# Revit family: Building-IEC309Connections-GEWISS-67IB-INTERLOCKED-SOCKET-OUTLETS_IP67_WITHOUT_BOTTOM_FUS
name_source: partatom
category: Apparecchi elettrici
revit_build: Autodesk Revit 2016 (Build: 20161004_0715(x64)
units: mm (PartAtom-declared; Revit-internal decimal feet)

## family parameters
Condiviso = No
Host = Muro
Mantenere orientamento annotazione = Sì
Numero OmniClass = 23.80.50.14
Punto di calcolo locali = No
Quota connettore circolare = Usa diametro
Sempre verticale = Sì
Taglio con vuoti quando caricato = No
Tipo di parte = Normale
Titolo OmniClass = Plug Connectors

## types (23) — shared parameters
Altezza da terra = 1112 mm
Carico apparente = 0 VA
Catalogue = BUILDING
Catalogue Range = 67 IB
Classificazione carico = Altro
Electrocod = 2222
Frequency = 50/60 Hz
Fuse breacking capacity = > 50 kA
Glow Wire Test = 850 °C
Glow wire test: = 850 °C
IDF = 7497af57-3216-4345-8823-f8ebadf7cf6f
IDT = 5410a18b-86cc-47a6-890a-93cf755ebe5d
IP degree = IP67
Immagine tipo = GW66329N.jpg
Numero poli = 3
Operating temperature: = -25 +40 °C
Potenza = 400 V
Presa = GW - ROSSO
Produttore = GEWISS S.p.A.
Protection = Fuse-holder base (CBF)
Rated frequency (Hz) = 50/60 Hz
Rated impulse withstand voltage = 4KV
Rated insulation voltage (Ui) = 500V
Rated short-circuit current (Icc) = 10KA
SEO = Socket outlet
Shock resistance = IK08
Struttura = GEWISS - Grigio RAL - 7035
Struttura frontale = GEWISS -BLU
Technical sheet = https://www.gewiss.com
Thermo-pressure with ball = 125
Tipo Simbolo = PRESAINDPFUS : 3P
Type of fuse = Ã˜ 10.3x38 mm
Typology = Vertical
URL = https://www.gewiss.com
Version file RFA = 18.0
Vetro = GEWISS - vetro
With back-mounting box = No
Working temperature = -25 ÷ +40 °C

## per-type parameters (varying)
| type | Colour | Colour: | Descrizione | EAN code | IB socket outlet rated current (In) | Modello | No. of poles | Number of poles | Rated current (A) | Rated current (In) | Rated voltage | Rated voltage: | Reference h | Weight | Weight (kg) |
| GW66339N - 32A 3P+N+E 230V V.INT.SOCK.O.N.B.9H CBF | Blue | Blue | 32A 3P+N+E 230V V.INT.SOCK.O.N.B.9H CBF | 8011564741942 | 28A | GW66339N | 3P+N+E | 3P+N+E | 32 | 32 | 200 - 250 V | 200 - 250 V | 9 | Max. 0.9 Kg | Max. 0.9 Kg |
| GW66343N - 32A 3P+E 500V V.INT.SOCK.O.N.B.7H CBF | Black | Black | 32A 3P+E 500V V.INT.SOCK.O.N.B.7H CBF | 8011564741980 | 28A | GW66343N | 3P+E | 3P+E | 32 | 32 | 480 - 500 V | 480 - 500 V | 7 | Max. 0.9 Kg | Max. 0.9 Kg |
| GW66358N - 32A 3P+E 380V V.INT.SOCK.O.N.B.3H CBF | Red | Red | 32A 3P+E 380V V.INT.SOCK.O.N.B.3H CBF | 8011564742123 | 28A | GW66358N | 3P+E | 3P+E | 32 | 32 | 380 - 440 V | 380 - 440 V | 3 | Max. 0.9 Kg | Max. 0.9 Kg |
| GW66327N - 16A 3P+E 230V V.INT.SOCK.O.N.B.9H CBF | Blue | Blue | 16A 3P+E 230V V.INT.SOCK.O.N.B.9H CBF | 8011564741829 | 16A | GW66327N | 3P+E | 3P+E | 16 | 16 | 200 - 250 V | 200 - 250 V | 9 | Max. 0.8 Kg | Max. 0.8 Kg |
| GW66333N - 16A 3P+N+E 500V V.INT.SOCK.O.N.B.7H CBF | Black | Black | 16A 3P+N+E 500V V.INT.SOCK.O.N.B.7H CBF | 8011564741881 | 16A | GW66333N | 3P+N+E | 3P+N+E | 16 | 16 | 480 - 500 V | 480 - 500 V | 7 | Max. 0.8 Kg | Max. 0.8 Kg |
| GW66328N - 16A 3P+N+E 230V V.INT.SOCK.O.N.B.9H CBF | Blue | Blue | 16A 3P+N+E 230V V.INT.SOCK.O.N.B.9H CBF | 8011564741836 | 16A | GW66328N | 3P+N+E | 3P+N+E | 16 | 16 | 200 - 250 V | 200 - 250 V | 9 | Max. 0.8 Kg | Max. 0.8 Kg |
| GW66324N - 16A 3P+E 110V V.INT.SOCK.O.N.B.4H CBF | Yellow | Yellow | 16A 3P+E 110V V.INT.SOCK.O.N.B.4H CBF | 8011564741799 | 16A | GW66324N | 3P+E | 3P+E | 16 | 16 | 100 - 130 V | 100 - 130 V | 4 | Max. 0.8 Kg | Max. 0.8 Kg |
| GW66325N - 16A 3P+N+E 110V V.INT.SOCK.O.N.B.4H CBF | Yellow | Yellow | 16A 3P+N+E 110V V.INT.SOCK.O.N.B.4H CBF | 8011564741805 | 16A | GW66325N | 3P+N+E | 3P+N+E | 16 | 16 | 100 - 130 V | 100 - 130 V | 4 | Max. 0.8 Kg | Max. 0.8 Kg |
| GW66340N - 32A 2P+E 400V V.INT.SOCK.O.N.B.6H CBF | Red | Red | 32A 2P+E 400V V.INT.SOCK.O.N.B.6H CBF | 8011564741959 | 32A | GW66340N | 2P+E | 2P+E | 32 | 32 | 380 - 415 V | 380 - 415 V | 9 | Max. 0.9 Kg | Max. 0.9 Kg |
| GW66342N - 32A 3P+N+E 400V V.INT.SOCK.O.N.B.9H CBF | Red | Red | 32A 3P+N+E 400V V.INT.SOCK.O.N.B.9H CBF | 8011564741973 | 28A | GW66342N | 3P+N+E | 3P+N+E | 32 | 32 | 380 - 415 V | 380 - 415 V | 6 | Max. 0.9 Kg | Max. 0.9 Kg |
| GW66344N - 32A 3P+N+E 500V V.INT.SOCK.O.N.B.7H CBF | Black | Black | 32A 3P+N+E 500V V.INT.SOCK.O.N.B.7H CBF | 8011564741997 | 28A | GW66344N | 3P+N+E | 3P+N+E | 32 | 32 | 480 - 500 V | 480 - 500 V | 7 | Max. 0.9 Kg | Max. 0.9 Kg |
| GW66332N - 16A 3P+E 500V V.INT.SOCK.O.N.B.7H CBF | Black | Black | 16A 3P+E 500V V.INT.SOCK.O.N.B.7H CBF | 8011564741874 | 16A | GW66332N | 3P+E | 3P+E | 16 | 16 | 480 - 500 V | 480 - 500 V | 7 | Max. 0.8 Kg | Max. 0.8 Kg |
| GW66331N - 16A 3P+N+E 400V V.INT.SOCK.O.N.B.9H CBF | Red | Red | 16A 3P+N+E 400V V.INT.SOCK.O.N.B.9H CBF | 8011564741867 | 16A | GW66331N | 3P+N+E | 3P+N+E | 16 | 16 | 380 - 415 V | 380 - 415 V | 6 | Max. 0.8 Kg | Max. 0.8 Kg |
| GW66334N - 32A 2P+E 110V V.INT.SOCK.O.N.B.4H CBF | Yellow | Yellow | 32A 2P+E 110V V.INT.SOCK.O.N.B.4H CBF | 8011564741898 | 32A | GW66334N | 2P+E | 2P+E | 32 | 32 | 100 - 130 V | 100 - 130 V | 4 | Max. 0.9 Kg | Max. 0.9 Kg |
| GW66335N - 32A 3P+E 110V V.INT.SOCK.O.N.B.4H CBF | Yellow | Yellow | 32A 3P+E 110V V.INT.SOCK.O.N.B.4H CBF | 8011564741904 | 28A | GW66335N | 3P+E | 3P+E | 32 | 32 | 100 - 130 V | 100 - 130 V | 4 | Max. 0.9 Kg | Max. 0.9 Kg |
| GW66330N - 16A 3P+E 400V V.INT.SOCK.O.N.B.9H CBF | Red | Red | 16A 3P+E 400V V.INT.SOCK.O.N.B.9H CBF | 8011564741850 | 16A | GW66330N | 3P+E | 3P+E | 16 | 16 | 380 - 415 V | 380 - 415 V | 6 | Max. 0.8 Kg | Max. 0.8 Kg |
| GW66329N - 16A 2P+E 400V V.INT.SOCK.O.N.B.6H CBF | Red | Red | 16A 2P+E 400V V.INT.SOCK.O.N.B.6H CBF | 8011564741843 | 16A | GW66329N | 2P+E | 2P+E | 16 | 16 | 380 - 415 V | 380 - 415 V | 9 | Max. 0.8 Kg | Max. 0.8 Kg |
| GW66337N - 32A 2P+E 230V V.INT.SOCK.O.N.B.6H CBF | Blue | Blue | 32A 2P+E 230V V.INT.SOCK.O.N.B.6H CBF | 8011564741928 | 32A | GW66337N | 2P+E | 2P+E | 32 | 32 | 200 - 250 V | 200 - 250 V | 6 | Max. 0.9 Kg | Max. 0.9 Kg |
| GW66338N - 32A 3P+E 230V V.INT.SOCK.O.N.B.9H CBF | Blue | Blue | 32A 3P+E 230V V.INT.SOCK.O.N.B.9H CBF | 8011564741935 | 28A | GW66338N | 3P+E | 3P+E | 32 | 32 | 200 - 250 V | 200 - 250 V | 9 | Max. 0.9 Kg | Max. 0.9 Kg |
| GW66323N - 16A 2P+E 110V V.INT.SOCK.O.N.B.4H CBF | Yellow | Yellow | 16A 2P+E 110V V.INT.SOCK.O.N.B.4H CBF | 8011564741782 | 16A | GW66323N | 2P+E | 2P+E | 16 | 16 | 100 - 130 V | 100 - 130 V | 4 | Max. 0.8 Kg | Max. 0.8 Kg |
| GW66326N - 16A 2P+E 230V V.INT.SOCK.O.N.B.6H CBF | Blue | Blue | 16A 2P+E 230V V.INT.SOCK.O.N.B.6H CBF | 8011564741812 | 16A | GW66326N | 2P+E | 2P+E | 16 | 16 | 200 - 250 V | 200 - 250 V | 6 | Max. 0.8 Kg | Max. 0.8 Kg |
| GW66341N - 32A 3P+E 400V V.INT.SOCK.O.N.B.9H CBF | Red | Red | 32A 3P+E 400V V.INT.SOCK.O.N.B.9H CBF | 8011564741966 | 28A | GW66341N | 3P+E | 3P+E | 32 | 32 | 380 - 415 V | 380 - 415 V | 6 | Max. 0.9 Kg | Max. 0.9 Kg |
| GW66336N - 32A 3P+N+E 110V V.INT.SOCK.O.N.B.4H CBF | Yellow | Yellow | 32A 3P+N+E 110V V.INT.SOCK.O.N.B.4H CBF | 8011564741911 | 28A | GW66336N | 3P+N+E | 3P+N+E | 32 | 32 | 100 - 130 V | 100 - 130 V | 4 | Max. 0.9 Kg | Max. 0.9 Kg |

note: source unit labels omitted for Thermo-pressure with ball — the stored unit's dimension contradicts the parameter name (converter mislabeling)

## geometry (parser evidence)
native form markers: Sweep x2
no freeform markers — native parametric forms only
